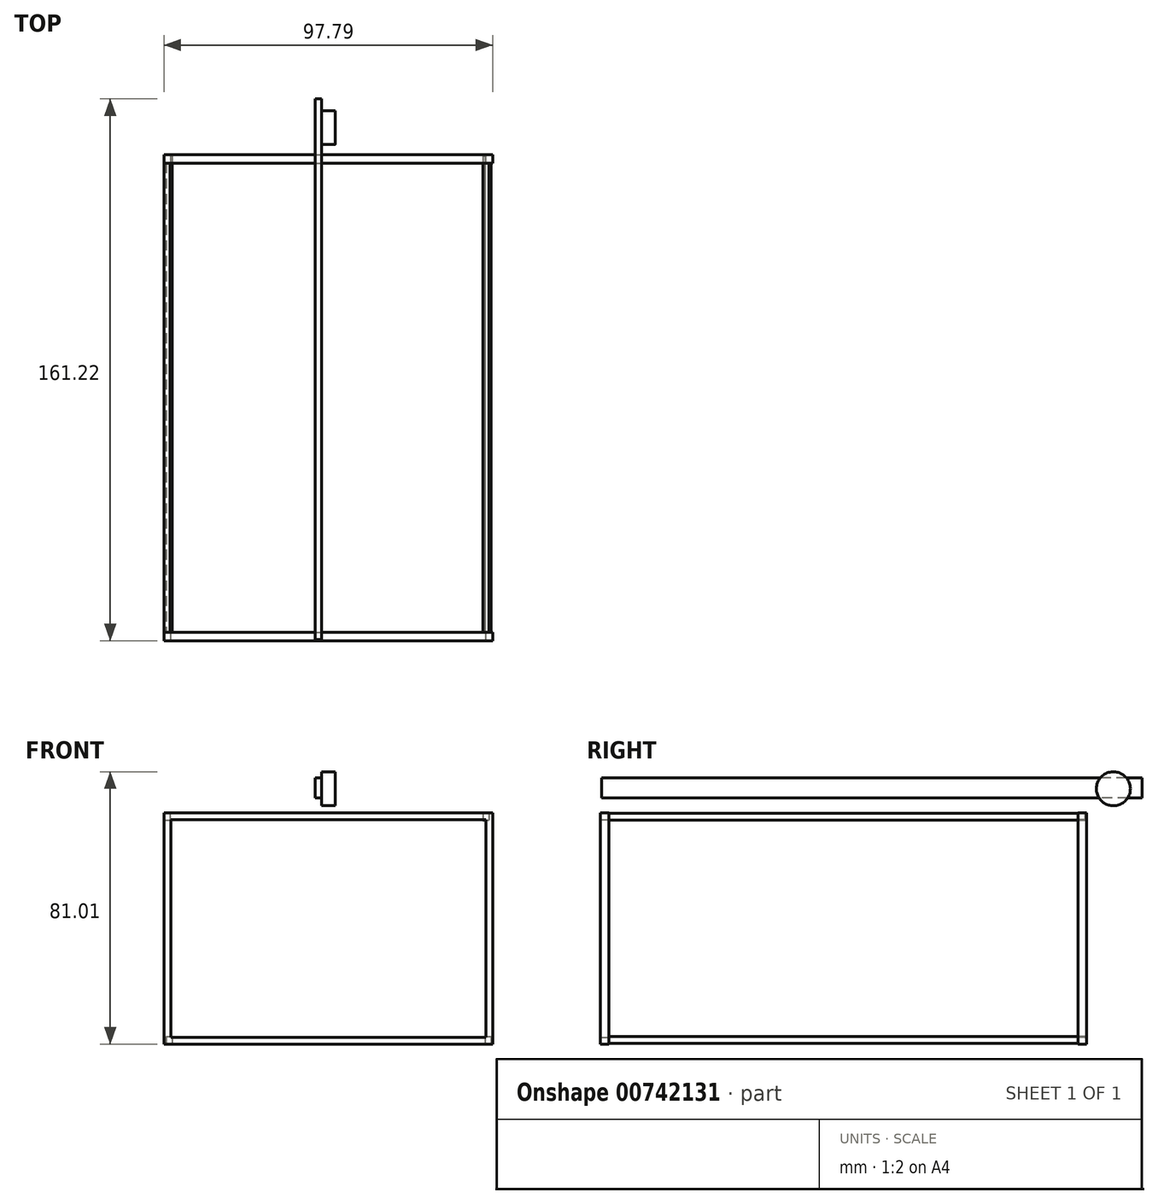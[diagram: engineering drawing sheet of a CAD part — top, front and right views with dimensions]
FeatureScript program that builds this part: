
annotation { "Feature Type Name" : "Feature", "Feature Type Description" : "" }
export const myFeature = defineFeature(function(context is Context, id is Id, definition is map)
    precondition{}
    {
        {
            var Q0;
            Q0=qCreatedBy(makeId("Front.planeOp"),FACE);
            var sketch = newSketch(context, id + "F0", { "sketchPlane" : qUnion([Q0])});
            skLineSegment(sketch, "E0.bottom", {"start": v(-46.83, 32.38) * mm, "end": v(46.83, 32.38) * mm});
            skLineSegment(sketch, "E0.top", {"start": v(-46.83, -32.38) * mm, "end": v(46.83, -32.38) * mm});
            skLineSegment(sketch, "E0.left", {"start": v(-46.83, 32.38) * mm, "end": v(-46.83, -32.38) * mm});
            skLineSegment(sketch, "E0.right", {"start": v(46.83, 32.38) * mm, "end": v(46.83, -32.38) * mm});
            skPoint(sketch, "E0.middle", {"position": v(0, 0) * mm});
            skLineSegment(sketch, "E1.0", {"start": v(-48.86, 34.41) * mm, "end": v(48.86, 34.41) * mm});
            skLineSegment(sketch, "E1.1", {"start": v(-48.86, 34.41) * mm, "end": v(-48.86, -34.41) * mm});
            skLineSegment(sketch, "E1.2", {"start": v(-48.86, -34.41) * mm, "end": v(48.86, -34.41) * mm});
            skLineSegment(sketch, "E1.3", {"start": v(48.86, 34.41) * mm, "end": v(48.86, -34.41) * mm});
            skSolve(sketch);
        }
        {
            var Q0;
            Q0 = qSketchRegion(id + "F0", true);
            extrude(context, id + "F1", {"entities" : qUnion([Q0]), "depth" : 2.54 * mm, "offsetDistance" : 25.4 * mm});
        }
        {
            var Q0;
            Q0=qCreatedBy(makeId("Top.planeOp"),FACE);
            var sketch = newSketch(context, id + "F2", { "sketchPlane" : qUnion([Q0])});
            skLineSegment(sketch, "E2", {"start": v(0, -73.27) * mm, "end": v(0, 68.83) * mm, "construction": true});
            skSolve(sketch);
        }
        {
            var Q0;
            Q0=makeQuery(id+"F1.opExtrude","SWEPT_BODY",BODY,{"disambiguationData":[OSD([sQuery(id+"F0.wireOp",EDGE,"E0.bottom"),sQuery(id+"F0.wireOp",EDGE,"E0.top"),sQuery(id+"F0.wireOp",EDGE,"E0.left"),sQuery(id+"F0.wireOp",EDGE,"E0.right"),sQuery(id+"F0.wireOp",EDGE,"E1.0"),sQuery(id+"F0.wireOp",EDGE,"E1.1"),sQuery(id+"F0.wireOp",EDGE,"E1.2"),sQuery(id+"F0.wireOp",EDGE,"E1.3")])]});
            var Q1;
            Q1=sQuery(id+"F2.wireOp",EDGE,"E2");
            transform(context, id + "F3", {"entities" : qUnion([Q0]), "transformType" : TransformType.TRANSLATION_ENTITY, "oppositeDirectionEntity" : false, "transformLine" : qUnion([Q1]), "makeCopy" : true});
        }
        {
            var Q0;
            Q0=makeQuery(id+"F1.opExtrude","SWEPT_BODY",BODY,{"disambiguationData":[OSD([sQuery(id+"F0.wireOp",EDGE,"E0.bottom"),sQuery(id+"F0.wireOp",EDGE,"E0.top"),sQuery(id+"F0.wireOp",EDGE,"E0.left"),sQuery(id+"F0.wireOp",EDGE,"E0.right"),sQuery(id+"F0.wireOp",EDGE,"E1.0"),sQuery(id+"F0.wireOp",EDGE,"E1.1"),sQuery(id+"F0.wireOp",EDGE,"E1.2"),sQuery(id+"F0.wireOp",EDGE,"E1.3")])]});
            var Q1;
            Q1=makeQuery(id+"F3.opPattern","COPY",BODY,{"derivedFrom":makeQuery(id+"F1.opExtrude","SWEPT_BODY",BODY,{"disambiguationData":[OSD([sQuery(id+"F0.wireOp",EDGE,"E0.bottom"),sQuery(id+"F0.wireOp",EDGE,"E0.top"),sQuery(id+"F0.wireOp",EDGE,"E0.left"),sQuery(id+"F0.wireOp",EDGE,"E0.right"),sQuery(id+"F0.wireOp",EDGE,"E1.0"),sQuery(id+"F0.wireOp",EDGE,"E1.1"),sQuery(id+"F0.wireOp",EDGE,"E1.2"),sQuery(id+"F0.wireOp",EDGE,"E1.3")])]}),"instanceName":"1"});
            var Q2;
            Q2=qCreatedBy(makeId("Front.planeOp"),FACE);
            transform(context, id + "F4", {"entities" : qUnion([Q0, Q1]), "transformType" : TransformType.TRANSLATION_DISTANCE, "transformDirection" : qUnion([Q2]), "distance" : 71 * mm, "makeCopy" : false});
        }
        {
            var Q0;
            Q0=qCreatedBy(makeId("Front.planeOp"),FACE);
            cPlane(context, id + "F5", {"entities" : qUnion([Q0]), "cplaneType" : CPlaneType.OFFSET, "offset" : 71 * mm, "width" : 150 * mm, "height" : 150 * mm});
        }
        {
            var Q0;
            Q0=qCreatedBy(id+"F5.planeOp",FACE);
            var sketch = newSketch(context, id + "F6", { "sketchPlane" : qUnion([Q0])});
            skLineSegment(sketch, "E3.bottom", {"start": v(46.63, -32.12) * mm, "end": v(48.4, -32.12) * mm});
            skLineSegment(sketch, "E3.top", {"start": v(46.63, -34.2) * mm, "end": v(48.4, -34.2) * mm});
            skLineSegment(sketch, "E3.left", {"start": v(46.63, -32.12) * mm, "end": v(46.63, -34.2) * mm});
            skLineSegment(sketch, "E3.right", {"start": v(48.4, -32.12) * mm, "end": v(48.4, -34.2) * mm});
            skLineSegment(sketch, "E4.0.1.0", {"start": v(47.78, 34.27) * mm, "end": v(47.78, 32.2) * mm});
            skLineSegment(sketch, "E4.0.1.1", {"start": v(46, 34.27) * mm, "end": v(46, 32.2) * mm});
            skLineSegment(sketch, "E4.0.1.2", {"start": v(46, 32.2) * mm, "end": v(47.78, 32.2) * mm});
            skLineSegment(sketch, "E4.0.1.3", {"start": v(46, 34.27) * mm, "end": v(47.78, 34.27) * mm});
            skLineSegment(sketch, "E4.1.0.0", {"start": v(-46.52, -32.13) * mm, "end": v(-46.52, -34.2) * mm});
            skLineSegment(sketch, "E4.1.0.1", {"start": v(-48.3, -32.13) * mm, "end": v(-48.3, -34.2) * mm});
            skLineSegment(sketch, "E4.1.0.2", {"start": v(-48.3, -34.2) * mm, "end": v(-46.52, -34.2) * mm});
            skLineSegment(sketch, "E4.1.0.3", {"start": v(-48.3, -32.13) * mm, "end": v(-46.52, -32.13) * mm});
            skLineSegment(sketch, "E4.1.1.0", {"start": v(-47.15, 34.27) * mm, "end": v(-47.15, 32.2) * mm});
            skLineSegment(sketch, "E4.1.1.1", {"start": v(-48.93, 34.27) * mm, "end": v(-48.93, 32.2) * mm});
            skLineSegment(sketch, "E4.1.1.2", {"start": v(-48.93, 32.2) * mm, "end": v(-47.15, 32.2) * mm});
            skLineSegment(sketch, "E4.1.1.3", {"start": v(-48.93, 34.27) * mm, "end": v(-47.15, 34.27) * mm});
            skLineSegment(sketch, "E4.direction1", {"start": v(46.63, -34.2) * mm, "end": v(-48.3, -34.2) * mm, "construction": true});
            skLineSegment(sketch, "E4.direction2", {"start": v(46.63, -34.2) * mm, "end": v(46, 32.2) * mm, "construction": true});
            skSolve(sketch);
        }
        {
            var Q0;
            Q0=makeQuery(id+"F6.imprint","IMPRINT",FACE,{"disambiguationData":[TD([[makeQuery(id+"F6.imprint","IMPRINT",EDGE,{"derivedFrom":sQuery(id+"F6.wireOp",EDGE,"E3.bottom")}),-1.0]])]});
            extrude(context, id + "F7", {"entities" : qUnion([Q0]), "operationType" : NewBodyOperationType.ADD, "oppositeDirection" : true, "depth" : 141.7 * mm, "offsetDistance" : 25 * mm});
        }
        {
            var Q0;
            Q0=makeQuery(id+"F6.imprint","IMPRINT",FACE,{"disambiguationData":[TD([[makeQuery(id+"F6.imprint","IMPRINT",EDGE,{"derivedFrom":sQuery(id+"F6.wireOp",EDGE,"E4.0.1.0")}),-1.0]])]});
            extrude(context, id + "F8", {"entities" : qUnion([Q0]), "operationType" : NewBodyOperationType.ADD, "oppositeDirection" : true, "depth" : 141.7 * mm, "offsetDistance" : 25 * mm});
        }
        {
            var Q0;
            Q0=makeQuery(id+"F6.imprint","IMPRINT",FACE,{"disambiguationData":[TD([[makeQuery(id+"F6.imprint","IMPRINT",EDGE,{"derivedFrom":sQuery(id+"F6.wireOp",EDGE,"E4.1.1.0")}),-1.0]])]});
            extrude(context, id + "F9", {"entities" : qUnion([Q0]), "operationType" : NewBodyOperationType.ADD, "oppositeDirection" : true, "depth" : 141.7 * mm, "offsetDistance" : 25 * mm});
        }
        {
            var Q0;
            Q0=makeQuery(id+"F6.imprint","IMPRINT",FACE,{"disambiguationData":[TD([[makeQuery(id+"F6.imprint","IMPRINT",EDGE,{"derivedFrom":sQuery(id+"F6.wireOp",EDGE,"E4.1.0.0")}),-1.0]])]});
            extrude(context, id + "F10", {"entities" : qUnion([Q0]), "operationType" : NewBodyOperationType.ADD, "oppositeDirection" : true, "depth" : 141.7 * mm, "offsetDistance" : 25 * mm});
        }
        {
            var Q0;
            Q0=qCreatedBy(makeId("Right.planeOp"),FACE);
            var sketch = newSketch(context, id + "F11", { "sketchPlane" : qUnion([Q0])});
            skCircle(sketch, "E5", {"center": v(79.12, 41.54) * mm, "radius": 5.06 * mm});
            skSolve(sketch);
        }
        {
            var Q0;
            Q0=makeQuery(id+"F11.imprint","IMPRINT",FACE,{"disambiguationData":[TD([[makeQuery(id+"F11.imprint","IMPRINT",EDGE,{"derivedFrom":sQuery(id+"F11.wireOp",EDGE,"E5")}),1.0]])]});
            var Q1;
            Q1=sQuery(id+"F11.wireOp",EDGE,"E5");
            extrude(context, id + "F12", {"entities" : qUnion([Q0]), "surfaceEntities" : qUnion([Q1]), "endBound" : BoundingType.SYMMETRIC, "depth" : 4 * mm, "offsetDistance" : 25 * mm});
        }
        {
            var Q0;
            Q0=makeQuery(id+"F12.opExtrude","CAP_FACE",FACE,{"disambiguationData":[OSD([sQuery(id+"F11.wireOp",EDGE,"E5")])],"isStart":true});
            var sketch = newSketch(context, id + "F13", { "sketchPlane" : qUnion([Q0])});
            skLineSegment(sketch, "E6.bottom", {"start": v(-87.68, 44.77) * mm, "end": v(73.17, 44.77) * mm});
            skLineSegment(sketch, "E6.top", {"start": v(-87.68, 38.8) * mm, "end": v(73.17, 38.8) * mm});
            skLineSegment(sketch, "E6.left", {"start": v(-87.68, 44.77) * mm, "end": v(-87.68, 38.8) * mm});
            skLineSegment(sketch, "E6.right", {"start": v(73.17, 44.77) * mm, "end": v(73.17, 38.8) * mm});
            skSolve(sketch);
        }
        {
            var Q0;
            Q0 = qSketchRegion(id + "F13", true);
            extrude(context, id + "F14", {"entities" : qUnion([Q0]), "operationType" : NewBodyOperationType.ADD, "depth" : 2 * mm, "offsetDistance" : 25 * mm});
        }
    });
